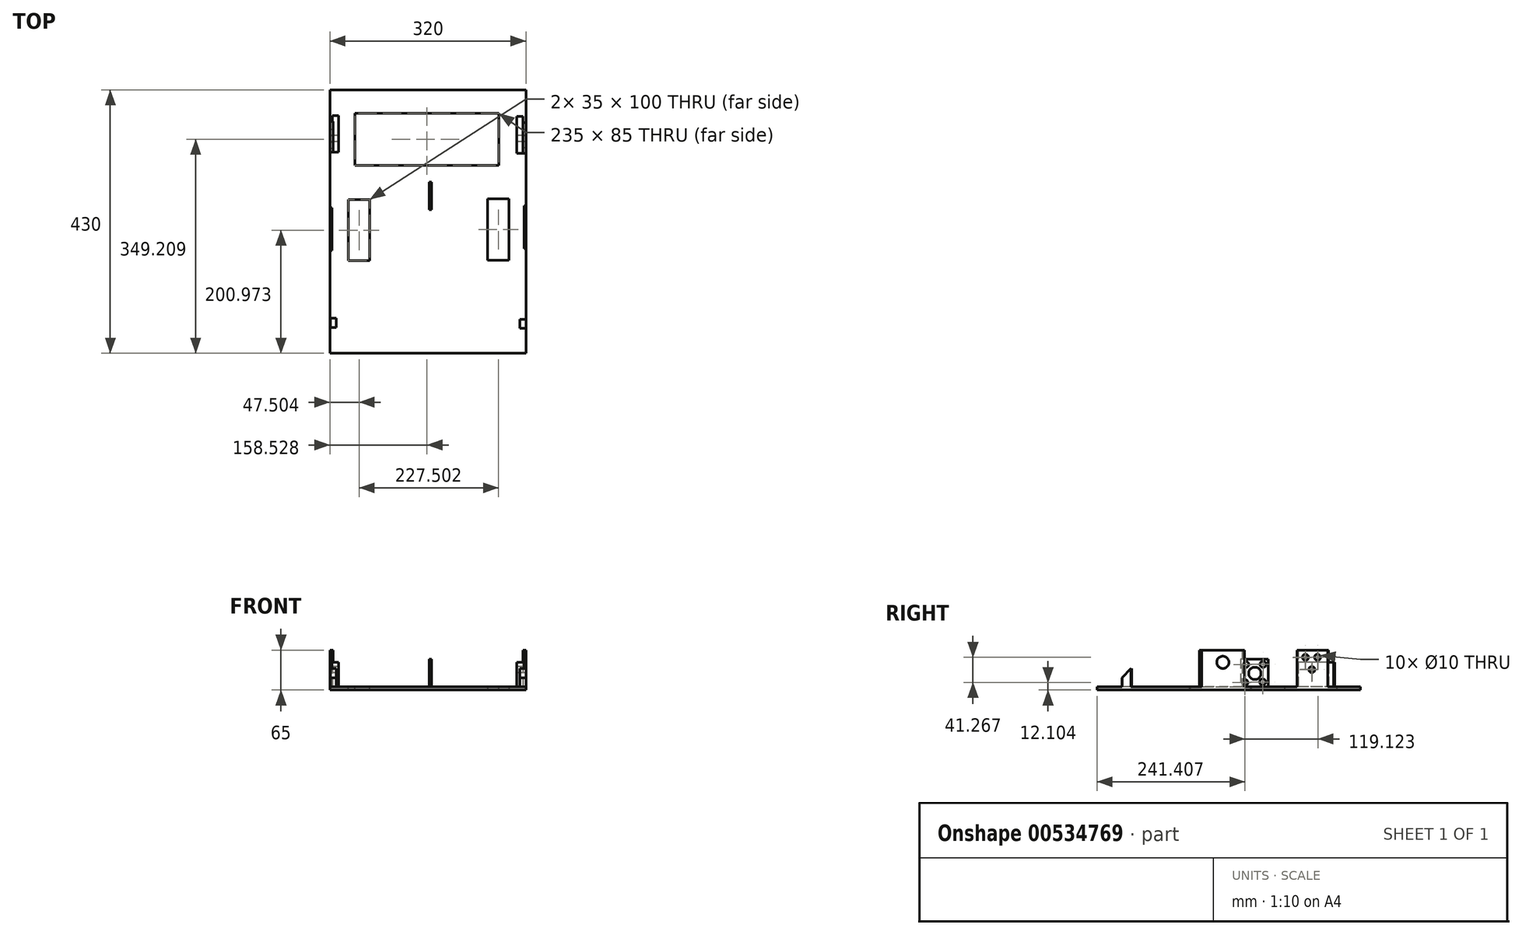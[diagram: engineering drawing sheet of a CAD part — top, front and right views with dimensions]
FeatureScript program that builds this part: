
annotation { "Feature Type Name" : "Feature", "Feature Type Description" : "" }
export const myFeature = defineFeature(function(context is Context, id is Id, definition is map)
    precondition{}
    {
        {
            var Q0;
            Q0=qCreatedBy(makeId("Top.planeOp"),FACE);
            var sketch = newSketch(context, id + "F0", { "sketchPlane" : qUnion([Q0])});
            skLineSegment(sketch, "E0.bottom", {"start": v(112.71, -29.67) * mm, "end": v(-207.29, -29.67) * mm});
            skLineSegment(sketch, "E0.top", {"start": v(112.71, 400.33) * mm, "end": v(-207.29, 400.33) * mm});
            skLineSegment(sketch, "E0.left", {"start": v(112.71, -29.67) * mm, "end": v(112.71, 400.33) * mm});
            skLineSegment(sketch, "E0.right", {"start": v(-207.29, -29.67) * mm, "end": v(-207.29, 400.33) * mm});
            skPoint(sketch, "E0.middle", {"position": v(-47.29, 185.33) * mm});
            skSolve(sketch);
        }
        {
            var Q0;
            Q0=makeQuery(id+"F0.imprint","IMPRINT",FACE,{"disambiguationData":[TD([[makeQuery(id+"F0.imprint","IMPRINT",EDGE,{"derivedFrom":sQuery(id+"F0.wireOp",EDGE,"E0.bottom")}),-1.0]])]});
            extrude(context, id + "F1", {"entities" : qUnion([Q0]), "depth" : 5 * mm});
        }
        {
            var Q0;
            Q0=makeQuery(id+"F1.opExtrude","CAP_FACE",FACE,{"disambiguationData":[OSD([sQuery(id+"F0.wireOp",EDGE,"E0.bottom"),sQuery(id+"F0.wireOp",EDGE,"E0.top"),sQuery(id+"F0.wireOp",EDGE,"E0.left"),sQuery(id+"F0.wireOp",EDGE,"E0.right")])],"isStart":false});
            var sketch = newSketch(context, id + "F2", { "sketchPlane" : qUnion([Q0])});
            skLineSegment(sketch, "E1.bottom", {"start": v(-142.29, 121.3) * mm, "end": v(-177.29, 121.3) * mm});
            skLineSegment(sketch, "E1.top", {"start": v(-142.29, 221.3) * mm, "end": v(-177.29, 221.3) * mm});
            skLineSegment(sketch, "E1.left", {"start": v(-142.29, 121.3) * mm, "end": v(-142.29, 221.3) * mm});
            skLineSegment(sketch, "E1.right", {"start": v(-177.29, 121.3) * mm, "end": v(-177.29, 221.3) * mm});
            skPoint(sketch, "E1.middle", {"position": v(-159.79, 171.3) * mm});
            skSolve(sketch);
        }
        {
            var Q0;
            Q0=qSketchRegion(id+"F2",true);
            extrude(context, id + "F3", {"entities" : qUnion([Q0]), "operationType" : NewBodyOperationType.REMOVE, "oppositeDirection" : true, "depth" : 5 * mm, "offsetDistance" : 25 * mm});
        }
        {
            var Q0;
            Q0=makeQuery(id+"F1.opExtrude","CAP_FACE",FACE,{"disambiguationData":[OSD([sQuery(id+"F0.wireOp",EDGE,"E0.bottom"),sQuery(id+"F0.wireOp",EDGE,"E0.top"),sQuery(id+"F0.wireOp",EDGE,"E0.left"),sQuery(id+"F0.wireOp",EDGE,"E0.right")])],"isStart":true});
            var sketch = newSketch(context, id + "F4", { "sketchPlane" : qUnion([Q0])});
            skLineSegment(sketch, "E2.bottom", {"start": v(50.22, -122.21) * mm, "end": v(85.22, -122.21) * mm});
            skLineSegment(sketch, "E2.top", {"start": v(50.22, -222.21) * mm, "end": v(85.22, -222.21) * mm});
            skLineSegment(sketch, "E2.left", {"start": v(50.22, -122.21) * mm, "end": v(50.22, -222.21) * mm});
            skLineSegment(sketch, "E2.right", {"start": v(85.22, -122.21) * mm, "end": v(85.22, -222.21) * mm});
            skPoint(sketch, "E2.middle", {"position": v(67.72, -172.21) * mm});
            skSolve(sketch);
        }
        {
            var Q0;
            Q0=qSketchRegion(id+"F4",true);
            extrude(context, id + "F5", {"entities" : qUnion([Q0]), "operationType" : NewBodyOperationType.REMOVE, "oppositeDirection" : true, "depth" : 5 * mm});
        }
        {
            var Q0;
            Q0=makeQuery(id+"F1.opExtrude","CAP_FACE",FACE,{"disambiguationData":[OSD([sQuery(id+"F0.wireOp",EDGE,"E0.bottom"),sQuery(id+"F0.wireOp",EDGE,"E0.top"),sQuery(id+"F0.wireOp",EDGE,"E0.left"),sQuery(id+"F0.wireOp",EDGE,"E0.right")])],"isStart":false});
            var sketch = newSketch(context, id + "F6", { "sketchPlane" : qUnion([Q0])});
            skLineSegment(sketch, "E3.bottom", {"start": v(-166.26, 362.04) * mm, "end": v(68.74, 362.04) * mm});
            skLineSegment(sketch, "E3.top", {"start": v(-166.26, 277.04) * mm, "end": v(68.74, 277.04) * mm});
            skLineSegment(sketch, "E3.left", {"start": v(-166.26, 362.04) * mm, "end": v(-166.26, 277.04) * mm});
            skLineSegment(sketch, "E3.right", {"start": v(68.74, 362.04) * mm, "end": v(68.74, 277.04) * mm});
            skLineSegment(sketch, "E4.bottom", {"start": v(-48.76, 277.04) * mm, "end": v(-65.01, 277.04) * mm});
            skLineSegment(sketch, "E4.top", {"start": v(-48.76, 277.04) * mm, "end": v(-65.01, 277.04) * mm});
            skLineSegment(sketch, "E4.left", {"start": v(-48.76, 277.04) * mm, "end": v(-48.76, 277.04) * mm});
            skLineSegment(sketch, "E4.right", {"start": v(-65.01, 277.04) * mm, "end": v(-65.01, 277.04) * mm});
            skSolve(sketch);
        }
        {
            var Q0;
            Q0=qSketchRegion(id+"F6",true);
            extrude(context, id + "F7", {"entities" : qUnion([Q0]), "operationType" : NewBodyOperationType.REMOVE, "oppositeDirection" : true, "depth" : 5 * mm});
        }
        {
            var Q0;
            Q0=makeQuery(id+"F1.opExtrude","CAP_FACE",FACE,{"disambiguationData":[OSD([sQuery(id+"F0.wireOp",EDGE,"E0.bottom"),sQuery(id+"F0.wireOp",EDGE,"E0.top"),sQuery(id+"F0.wireOp",EDGE,"E0.left"),sQuery(id+"F0.wireOp",EDGE,"E0.right")])],"isStart":false});
            var sketch = newSketch(context, id + "F8", { "sketchPlane" : qUnion([Q0])});
            skLineSegment(sketch, "E5.bottom", {"start": v(-207.29, 207.67) * mm, "end": v(-204.29, 207.67) * mm});
            skLineSegment(sketch, "E5.top", {"start": v(-207.29, 137.67) * mm, "end": v(-204.29, 137.67) * mm});
            skLineSegment(sketch, "E5.left", {"start": v(-207.29, 207.67) * mm, "end": v(-207.29, 137.67) * mm});
            skLineSegment(sketch, "E5.right", {"start": v(-204.29, 207.67) * mm, "end": v(-204.29, 137.67) * mm});
            skSolve(sketch);
        }
        {
            var Q0;
            Q0=qSketchRegion(id+"F8",true);
            extrude(context, id + "F9", {"entities" : qUnion([Q0]), "operationType" : NewBodyOperationType.ADD, "depth" : 60 * mm});
        }
        {
            var Q0;
            Q0=makeQuery(id+"F1.opExtrude","CAP_FACE",FACE,{"disambiguationData":[OSD([sQuery(id+"F0.wireOp",EDGE,"E0.bottom"),sQuery(id+"F0.wireOp",EDGE,"E0.top"),sQuery(id+"F0.wireOp",EDGE,"E0.left"),sQuery(id+"F0.wireOp",EDGE,"E0.right")])],"isStart":false});
            var sketch = newSketch(context, id + "F10", { "sketchPlane" : qUnion([Q0])});
            skLineSegment(sketch, "E6.bottom", {"start": v(112.71, 211.3) * mm, "end": v(109.71, 211.3) * mm});
            skLineSegment(sketch, "E6.top", {"start": v(112.71, 141.3) * mm, "end": v(109.71, 141.3) * mm});
            skLineSegment(sketch, "E6.left", {"start": v(112.71, 211.3) * mm, "end": v(112.71, 141.3) * mm});
            skLineSegment(sketch, "E6.right", {"start": v(109.71, 211.3) * mm, "end": v(109.71, 141.3) * mm});
            skSolve(sketch);
        }
        {
            var Q0;
            Q0=qSketchRegion(id+"F10",true);
            extrude(context, id + "F11", {"entities" : qUnion([Q0]), "operationType" : NewBodyOperationType.ADD, "depth" : 60 * mm});
        }
        {
            var Q0;
            Q0=makeQuery(id+"F1.opExtrude","CAP_FACE",FACE,{"disambiguationData":[OSD([sQuery(id+"F0.wireOp",EDGE,"E0.bottom"),sQuery(id+"F0.wireOp",EDGE,"E0.top"),sQuery(id+"F0.wireOp",EDGE,"E0.left"),sQuery(id+"F0.wireOp",EDGE,"E0.right")])],"isStart":false});
            var sketch = newSketch(context, id + "F12", { "sketchPlane" : qUnion([Q0])});
            skLineSegment(sketch, "E7.bottom", {"start": v(-207.29, 348.58) * mm, "end": v(-202.29, 348.58) * mm});
            skLineSegment(sketch, "E7.top", {"start": v(-207.29, 298.58) * mm, "end": v(-202.29, 298.58) * mm});
            skLineSegment(sketch, "E7.left", {"start": v(-207.29, 348.58) * mm, "end": v(-207.29, 298.58) * mm});
            skLineSegment(sketch, "E7.right", {"start": v(-202.29, 348.58) * mm, "end": v(-202.29, 298.58) * mm});
            skSolve(sketch);
        }
        {
            var Q0;
            Q0=qSketchRegion(id+"F12",true);
            extrude(context, id + "F13", {"entities" : qUnion([Q0]), "operationType" : NewBodyOperationType.ADD, "depth" : 60 * mm, "offsetDistance" : 25 * mm});
        }
        {
            var Q0;
            Q0=makeQuery(id+"F1.opExtrude","CAP_FACE",FACE,{"disambiguationData":[OSD([sQuery(id+"F0.wireOp",EDGE,"E0.bottom"),sQuery(id+"F0.wireOp",EDGE,"E0.top"),sQuery(id+"F0.wireOp",EDGE,"E0.left"),sQuery(id+"F0.wireOp",EDGE,"E0.right")])],"isStart":false});
            var sketch = newSketch(context, id + "F14", { "sketchPlane" : qUnion([Q0])});
            skLineSegment(sketch, "E8.bottom", {"start": v(112.71, 346.76) * mm, "end": v(107.71, 346.76) * mm});
            skLineSegment(sketch, "E8.top", {"start": v(112.71, 296.76) * mm, "end": v(107.71, 296.76) * mm});
            skLineSegment(sketch, "E8.left", {"start": v(112.71, 346.76) * mm, "end": v(112.71, 296.76) * mm});
            skLineSegment(sketch, "E8.right", {"start": v(107.71, 346.76) * mm, "end": v(107.71, 296.76) * mm});
            skSolve(sketch);
        }
        {
            var Q0;
            Q0=qSketchRegion(id+"F14",true);
            extrude(context, id + "F15", {"entities" : qUnion([Q0]), "operationType" : NewBodyOperationType.ADD, "depth" : 60 * mm});
        }
        {
            var Q0;
            Q0=qCreatedBy(makeId("Right.planeOp"),FACE);
            var sketch = newSketch(context, id + "F16", { "sketchPlane" : qUnion([Q0])});
            skCircle(sketch, "E9", {"center": v(175.78, 45.06) * mm, "radius": 10 * mm});
            skSolve(sketch);
        }
        {
            var Q0;
            Q0=qSketchRegion(id+"F16",true);
            extrude(context, id + "F17", {"entities" : qUnion([Q0]), "operationType" : NewBodyOperationType.REMOVE, "depth" : 120 * mm});
        }
        {
            var Q0;
            Q0=qCreatedBy(makeId("Right.planeOp"),FACE);
            var sketch = newSketch(context, id + "F18", { "sketchPlane" : qUnion([Q0])});
            skCircle(sketch, "E10", {"center": v(176.23, 45.3) * mm, "radius": 10.26 * mm});
            skSolve(sketch);
        }
        {
            var Q0;
            Q0=qSketchRegion(id+"F18",true);
            extrude(context, id + "F19", {"entities" : qUnion([Q0]), "operationType" : NewBodyOperationType.REMOVE, "oppositeDirection" : true, "depth" : 240 * mm});
        }
        {
            var Q0;
            Q0=makeQuery(id+"F1.opExtrude","CAP_FACE",FACE,{"disambiguationData":[OSD([sQuery(id+"F0.wireOp",EDGE,"E0.bottom"),sQuery(id+"F0.wireOp",EDGE,"E0.top"),sQuery(id+"F0.wireOp",EDGE,"E0.left"),sQuery(id+"F0.wireOp",EDGE,"E0.right")])],"isStart":false});
            var sketch = newSketch(context, id + "F20", { "sketchPlane" : qUnion([Q0])});
            skLineSegment(sketch, "E11.bottom", {"start": v(102.71, 25.85) * mm, "end": v(112.71, 25.85) * mm});
            skLineSegment(sketch, "E11.top", {"start": v(102.71, 10.85) * mm, "end": v(112.71, 10.85) * mm});
            skLineSegment(sketch, "E11.left", {"start": v(102.71, 25.85) * mm, "end": v(102.71, 10.85) * mm});
            skLineSegment(sketch, "E11.right", {"start": v(112.71, 25.85) * mm, "end": v(112.71, 10.85) * mm});
            skSolve(sketch);
        }
        {
            var Q0;
            Q0=qSketchRegion(id+"F20",true);
            extrude(context, id + "F21", {"entities" : qUnion([Q0]), "operationType" : NewBodyOperationType.ADD, "depth" : 30 * mm});
        }
        {
            var Q0;
            Q0=makeQuery(id+"F21.opExtrude","CAP_EDGE",EDGE,{"disambiguationData":[OSD([sQuery(id+"F20.wireOp",EDGE,"E11.top")])],"isStart":false});
            chamfer(context, id + "F22", {"entities" : qUnion([Q0]), "width" : 15 * mm, "tangentPropagation" : true});
        }
        {
            var Q0;
            {var subQ14=sQuery(id+"F20.wireOp",EDGE,"E11.bottom");Q0=makeQuery(id+"F20.imprint","IMPRINT",FACE,{"disambiguationData":[TD([[makeQuery(id+"F20.imprint","IMPRINT",EDGE,{"derivedFrom":subQ14}),1.0]])]});}
            var sketch = newSketch(context, id + "F23", { "sketchPlane" : qUnion([Q0])});
            skLineSegment(sketch, "E12.bottom", {"start": v(-206.83, 27.2) * mm, "end": v(-196.83, 27.2) * mm});
            skLineSegment(sketch, "E12.top", {"start": v(-206.83, 12.2) * mm, "end": v(-196.83, 12.2) * mm});
            skLineSegment(sketch, "E12.left", {"start": v(-206.83, 27.2) * mm, "end": v(-206.83, 12.2) * mm});
            skLineSegment(sketch, "E12.right", {"start": v(-196.83, 27.2) * mm, "end": v(-196.83, 12.2) * mm});
            skSolve(sketch);
        }
        {
            var Q0;
            Q0=qSketchRegion(id+"F23",true);
            extrude(context, id + "F24", {"entities" : qUnion([Q0]), "operationType" : NewBodyOperationType.ADD, "depth" : 30 * mm});
        }
        {
            var Q0;
            Q0=makeQuery(id+"F24.opExtrude","CAP_EDGE",EDGE,{"disambiguationData":[OSD([sQuery(id+"F23.wireOp",EDGE,"E12.top")])],"isStart":false});
            chamfer(context, id + "F25", {"entities" : qUnion([Q0]), "width" : 15 * mm, "tangentPropagation" : true});
        }
        {
            var Q0;
            Q0=makeQuery(id+"F1.opExtrude","CAP_FACE",FACE,{"disambiguationData":[OSD([sQuery(id+"F0.wireOp",EDGE,"E0.bottom"),sQuery(id+"F0.wireOp",EDGE,"E0.top"),sQuery(id+"F0.wireOp",EDGE,"E0.left"),sQuery(id+"F0.wireOp",EDGE,"E0.right")])],"isStart":false});
            var sketch = newSketch(context, id + "F26", { "sketchPlane" : qUnion([Q0])});
            skLineSegment(sketch, "E13.bottom", {"start": v(-45.38, 249.94) * mm, "end": v(-41.38, 249.94) * mm});
            skLineSegment(sketch, "E13.top", {"start": v(-45.38, 204.94) * mm, "end": v(-41.38, 204.94) * mm});
            skLineSegment(sketch, "E13.left", {"start": v(-45.38, 249.94) * mm, "end": v(-45.38, 204.94) * mm});
            skLineSegment(sketch, "E13.right", {"start": v(-41.38, 249.94) * mm, "end": v(-41.38, 204.94) * mm});
            skSolve(sketch);
        }
        {
            var Q0;
            Q0=qSketchRegion(id+"F26",true);
            extrude(context, id + "F27", {"entities" : qUnion([Q0]), "operationType" : NewBodyOperationType.ADD, "depth" : 45 * mm, "offsetDistance" : 25 * mm});
        }
        {
            var Q0;
            Q0=makeQuery(id+"F1.opExtrude","CAP_FACE",FACE,{"disambiguationData":[OSD([sQuery(id+"F0.wireOp",EDGE,"E0.bottom"),sQuery(id+"F0.wireOp",EDGE,"E0.top"),sQuery(id+"F0.wireOp",EDGE,"E0.left"),sQuery(id+"F0.wireOp",EDGE,"E0.right")])],"isStart":false});
            var sketch = newSketch(context, id + "F28", { "sketchPlane" : qUnion([Q0])});
            skLineSegment(sketch, "E14.bottom", {"start": v(97.71, 356.76) * mm, "end": v(107.71, 356.76) * mm});
            skLineSegment(sketch, "E14.top", {"start": v(97.71, 296.76) * mm, "end": v(107.71, 296.76) * mm});
            skLineSegment(sketch, "E14.left", {"start": v(97.71, 356.76) * mm, "end": v(97.71, 296.76) * mm});
            skLineSegment(sketch, "E14.right", {"start": v(107.71, 356.76) * mm, "end": v(107.71, 296.76) * mm});
            skSolve(sketch);
        }
        {
            var Q0;
            Q0=qSketchRegion(id+"F28",true);
            extrude(context, id + "F29", {"entities" : qUnion([Q0]), "operationType" : NewBodyOperationType.ADD, "depth" : 40 * mm, "offsetDistance" : 25 * mm});
        }
        {
            var Q0;
            Q0=makeQuery(id+"F1.opExtrude","CAP_FACE",FACE,{"disambiguationData":[OSD([sQuery(id+"F0.wireOp",EDGE,"E0.bottom"),sQuery(id+"F0.wireOp",EDGE,"E0.top"),sQuery(id+"F0.wireOp",EDGE,"E0.left"),sQuery(id+"F0.wireOp",EDGE,"E0.right")])],"isStart":false});
            var sketch = newSketch(context, id + "F30", { "sketchPlane" : qUnion([Q0])});
            skLineSegment(sketch, "E15.bottom", {"start": v(-203.2, 358.58) * mm, "end": v(-193.2, 358.58) * mm});
            skLineSegment(sketch, "E15.top", {"start": v(-203.2, 298.58) * mm, "end": v(-193.2, 298.58) * mm});
            skLineSegment(sketch, "E15.left", {"start": v(-203.2, 358.58) * mm, "end": v(-203.2, 298.58) * mm});
            skLineSegment(sketch, "E15.right", {"start": v(-193.2, 358.58) * mm, "end": v(-193.2, 298.58) * mm});
            skSolve(sketch);
        }
        {
            var Q0;
            Q0=qSketchRegion(id+"F30",true);
            extrude(context, id + "F31", {"entities" : qUnion([Q0]), "operationType" : NewBodyOperationType.ADD, "depth" : 40 * mm, "offsetDistance" : 25 * mm});
        }
        {
            var Q0;
            Q0=qCreatedBy(makeId("Right.planeOp"),FACE);
            var sketch = newSketch(context, id + "F32", { "sketchPlane" : qUnion([Q0])});
            skCircle(sketch, "E16", {"center": v(310.66, 53.37) * mm, "radius": 5 * mm});
            skSolve(sketch);
        }
        {
            var Q0;
            Q0=qSketchRegion(id+"F32",true);
            extrude(context, id + "F33", {"entities" : qUnion([Q0]), "operationType" : NewBodyOperationType.REMOVE, "depth" : 240 * mm, "offsetDistance" : 25 * mm});
        }
        {
            var Q0;
            Q0=qCreatedBy(makeId("Right.planeOp"),FACE);
            var sketch = newSketch(context, id + "F34", { "sketchPlane" : qUnion([Q0])});
            skCircle(sketch, "E17", {"center": v(330.28, 53.37) * mm, "radius": 5 * mm});
            skSolve(sketch);
        }
        {
            var Q0;
            Q0=qSketchRegion(id+"F34",true);
            extrude(context, id + "F35", {"entities" : qUnion([Q0]), "operationType" : NewBodyOperationType.REMOVE, "depth" : 240 * mm, "offsetDistance" : 25 * mm});
        }
        {
            var Q0;
            Q0=qCreatedBy(makeId("Right.planeOp"),FACE);
            var sketch = newSketch(context, id + "F36", { "sketchPlane" : qUnion([Q0])});
            skCircle(sketch, "E18", {"center": v(321.05, 33.18) * mm, "radius": 5 * mm});
            skSolve(sketch);
        }
        {
            var Q0;
            Q0=qSketchRegion(id+"F36",true);
            extrude(context, id + "F37", {"entities" : qUnion([Q0]), "operationType" : NewBodyOperationType.REMOVE, "depth" : 250 * mm, "offsetDistance" : 25 * mm});
        }
        {
            var Q0;
            Q0=qCreatedBy(makeId("Right.planeOp"),FACE);
            var sketch = newSketch(context, id + "F38", { "sketchPlane" : qUnion([Q0])});
            skCircle(sketch, "E19", {"center": v(310.09, 52.8) * mm, "radius": 5 * mm});
            skSolve(sketch);
        }
        {
            var Q0;
            Q0=qSketchRegion(id+"F38",true);
            extrude(context, id + "F39", {"entities" : qUnion([Q0]), "operationType" : NewBodyOperationType.REMOVE, "oppositeDirection" : true, "depth" : 300 * mm, "offsetDistance" : 25 * mm});
        }
        {
            var Q0;
            Q0=qCreatedBy(makeId("Right.planeOp"),FACE);
            var sketch = newSketch(context, id + "F40", { "sketchPlane" : qUnion([Q0])});
            skCircle(sketch, "E20", {"center": v(330.86, 53.37) * mm, "radius": 5 * mm});
            skSolve(sketch);
        }
        {
            var Q0;
            Q0=qSketchRegion(id+"F40",true);
            extrude(context, id + "F41", {"entities" : qUnion([Q0]), "operationType" : NewBodyOperationType.REMOVE, "oppositeDirection" : true, "depth" : 300 * mm, "offsetDistance" : 25 * mm});
        }
        {
            var Q0;
            Q0=qCreatedBy(makeId("Right.planeOp"),FACE);
            var sketch = newSketch(context, id + "F42", { "sketchPlane" : qUnion([Q0])});
            skCircle(sketch, "E21", {"center": v(321.63, 33.75) * mm, "radius": 5 * mm});
            skSolve(sketch);
        }
        {
            var Q0;
            Q0=qSketchRegion(id+"F42",true);
            extrude(context, id + "F43", {"entities" : qUnion([Q0]), "operationType" : NewBodyOperationType.REMOVE, "oppositeDirection" : true, "depth" : 300 * mm, "offsetDistance" : 25 * mm});
        }
        {
            var Q0;
            Q0=qCreatedBy(makeId("Right.planeOp"),FACE);
            var sketch = newSketch(context, id + "F44", { "sketchPlane" : qUnion([Q0])});
            skCircle(sketch, "E22", {"center": v(228, 27.1) * mm, "radius": 10 * mm});
            skSolve(sketch);
        }
        {
            var Q0;
            Q0=qSketchRegion(id+"F44",true);
            extrude(context, id + "F45", {"entities" : qUnion([Q0]), "operationType" : NewBodyOperationType.REMOVE, "endBound" : BoundingType.THROUGH_ALL, "oppositeDirection" : true, "depth" : 40 * mm, "offsetDistance" : 25 * mm});
        }
        {
            var Q0;
            Q0=qCreatedBy(makeId("Right.planeOp"),FACE);
            var sketch = newSketch(context, id + "F46", { "sketchPlane" : qUnion([Q0])});
            skCircle(sketch, "E23", {"center": v(241.43, 41.83) * mm, "radius": 5 * mm});
            skSolve(sketch);
        }
        {
            var Q0;
            Q0=qSketchRegion(id+"F46",true);
            extrude(context, id + "F47", {"entities" : qUnion([Q0]), "operationType" : NewBodyOperationType.REMOVE, "endBound" : BoundingType.THROUGH_ALL, "oppositeDirection" : true, "depth" : 25 * mm, "offsetDistance" : 25 * mm});
        }
        {
            var Q0;
            Q0=qCreatedBy(makeId("Right.planeOp"),FACE);
            var sketch = newSketch(context, id + "F48", { "sketchPlane" : qUnion([Q0])});
            skCircle(sketch, "E24", {"center": v(240.85, 12.98) * mm, "radius": 5 * mm});
            skSolve(sketch);
        }
        {
            var Q0;
            Q0=qSketchRegion(id+"F48",true);
            extrude(context, id + "F49", {"entities" : qUnion([Q0]), "operationType" : NewBodyOperationType.REMOVE, "endBound" : BoundingType.THROUGH_ALL, "oppositeDirection" : true, "depth" : 25 * mm, "offsetDistance" : 25 * mm});
        }
        {
            var Q0;
            Q0=qCreatedBy(makeId("Right.planeOp"),FACE);
            var sketch = newSketch(context, id + "F50", { "sketchPlane" : qUnion([Q0])});
            skCircle(sketch, "E25", {"center": v(213.08, 41.62) * mm, "radius": 5 * mm});
            skSolve(sketch);
        }
        {
            var Q0;
            Q0=qSketchRegion(id+"F50",true);
            extrude(context, id + "F51", {"entities" : qUnion([Q0]), "operationType" : NewBodyOperationType.REMOVE, "endBound" : BoundingType.THROUGH_ALL, "oppositeDirection" : true, "depth" : 25 * mm, "offsetDistance" : 25 * mm});
        }
        {
            var Q0;
            Q0=qCreatedBy(makeId("Right.planeOp"),FACE);
            var sketch = newSketch(context, id + "F52", { "sketchPlane" : qUnion([Q0])});
            skCircle(sketch, "E26", {"center": v(211.74, 12.1) * mm, "radius": 5 * mm});
            skSolve(sketch);
        }
        {
            var Q0;
            Q0=qSketchRegion(id+"F52",true);
            extrude(context, id + "F53", {"entities" : qUnion([Q0]), "operationType" : NewBodyOperationType.REMOVE, "endBound" : BoundingType.THROUGH_ALL, "oppositeDirection" : true, "depth" : 25 * mm, "offsetDistance" : 25 * mm});
        }
    });
